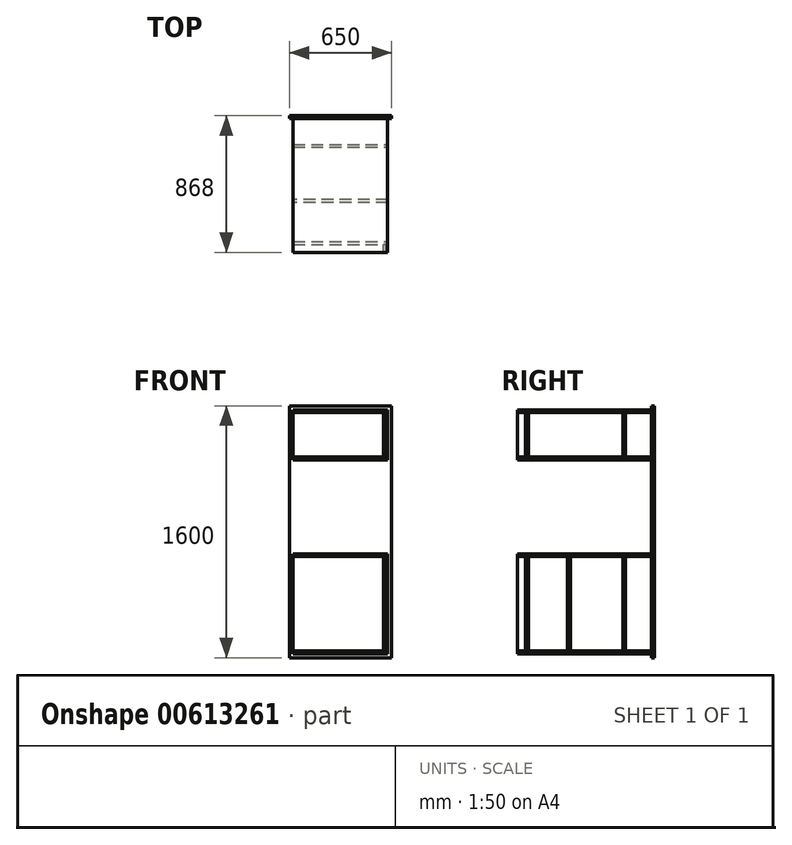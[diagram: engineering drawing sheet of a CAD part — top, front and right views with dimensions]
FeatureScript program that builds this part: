
annotation { "Feature Type Name" : "Feature", "Feature Type Description" : "" }
export const myFeature = defineFeature(function(context is Context, id is Id, definition is map)
    precondition{}
    {
        {
            var Q0;
            Q0=qCreatedBy(makeId("Top.planeOp"),FACE);
            var sketch = newSketch(context, id + "F0", { "sketchPlane" : qUnion([Q0])});
            skLineSegment(sketch, "E0.bottom", {"start": v(-313.84, 645.81) * mm, "end": v(286.16, 645.81) * mm});
            skLineSegment(sketch, "E0.top", {"start": v(-313.84, -204.19) * mm, "end": v(286.16, -204.19) * mm});
            skLineSegment(sketch, "E0.left", {"start": v(-313.84, 645.81) * mm, "end": v(-313.84, -204.19) * mm});
            skLineSegment(sketch, "E0.right", {"start": v(286.16, 645.81) * mm, "end": v(286.16, -204.19) * mm});
            skSolve(sketch);
        }
        {
            var Q0;
            Q0 = qSketchRegion(id + "F0", true);
            extrude(context, id + "F1", {"entities" : qUnion([Q0]), "depth" : 18 * mm, "offsetDistance" : 25 * mm});
        }
        {
            var Q0;
            Q0=makeQuery(id+"F1.opExtrude","SWEPT_FACE",FACE,{"disambiguationData":[OSD([sQuery(id+"F0.wireOp",EDGE,"E0.bottom")])]});
            var sketch = newSketch(context, id + "F2", { "sketchPlane" : qUnion([Q0])});
            skLineSegment(sketch, "E1.bottom", {"start": v(-311.16, 343) * mm, "end": v(338.84, 343) * mm});
            skLineSegment(sketch, "E1.top", {"start": v(-311.16, -1257) * mm, "end": v(338.84, -1257) * mm});
            skLineSegment(sketch, "E1.left", {"start": v(-311.16, 343) * mm, "end": v(-311.16, -1257) * mm});
            skLineSegment(sketch, "E1.right", {"start": v(338.84, 343) * mm, "end": v(338.84, -1257) * mm});
            skSolve(sketch);
        }
        {
            var Q0;
            Q0 = qSketchRegion(id + "F2", true);
            extrude(context, id + "F3", {"entities" : qUnion([Q0]), "depth" : 18 * mm, "offsetDistance" : 25 * mm});
        }
        {
            var Q0;
            Q0=makeQuery(id+"F3.opExtrude","CAP_FACE",FACE,{"disambiguationData":[OSD([sQuery(id+"F2.wireOp",EDGE,"E1.bottom"),sQuery(id+"F2.wireOp",EDGE,"E1.top"),sQuery(id+"F2.wireOp",EDGE,"E1.left"),sQuery(id+"F2.wireOp",EDGE,"E1.right")])],"isStart":true});
            var sketch = newSketch(context, id + "F4", { "sketchPlane" : qUnion([Q0])});
            skLineSegment(sketch, "E2.bottom", {"start": v(-313.84, -596) * mm, "end": v(286.16, -596) * mm});
            skLineSegment(sketch, "E2.top", {"start": v(-313.84, -614) * mm, "end": v(286.16, -614) * mm});
            skLineSegment(sketch, "E2.left", {"start": v(-313.84, -596) * mm, "end": v(-313.84, -614) * mm});
            skLineSegment(sketch, "E2.right", {"start": v(286.16, -596) * mm, "end": v(286.16, -614) * mm});
            skLineSegment(sketch, "E3.bottom", {"start": v(-313.84, -1214) * mm, "end": v(286.16, -1214) * mm});
            skLineSegment(sketch, "E3.top", {"start": v(-313.84, -1232) * mm, "end": v(286.16, -1232) * mm});
            skLineSegment(sketch, "E3.left", {"start": v(-313.84, -1214) * mm, "end": v(-313.84, -1232) * mm});
            skLineSegment(sketch, "E3.right", {"start": v(286.16, -1214) * mm, "end": v(286.16, -1232) * mm});
            skLineSegment(sketch, "E4.bottom", {"start": v(-313.84, 318) * mm, "end": v(286.16, 318) * mm});
            skLineSegment(sketch, "E4.top", {"start": v(-313.84, 300) * mm, "end": v(286.16, 300) * mm});
            skLineSegment(sketch, "E4.left", {"start": v(-313.84, 318) * mm, "end": v(-313.84, 300) * mm});
            skLineSegment(sketch, "E4.right", {"start": v(286.16, 318) * mm, "end": v(286.16, 300) * mm});
            skSolve(sketch);
        }
        {
            var Q0;
            Q0 = qSketchRegion(id + "F4", true);
            var Q1;
            Q1=makeQuery(id+"F1.opExtrude","SWEPT_FACE",FACE,{"disambiguationData":[OSD([sQuery(id+"F0.wireOp",EDGE,"E0.top")])]});
            extrude(context, id + "F5", {"entities" : qUnion([Q0]), "endBound" : BoundingType.UP_TO_SURFACE, "depth" : 25 * mm, "endBoundEntityFace" : qUnion([Q1]), "offsetDistance" : 25 * mm});
        }
        {
            var Q0;
            Q0=makeQuery(id+"F5.opExtrude","SWEPT_FACE",FACE,{"disambiguationData":[OSD([sQuery(id+"F4.wireOp",EDGE,"E3.bottom")])]});
            var sketch = newSketch(context, id + "F6", { "sketchPlane" : qUnion([Q0])});
            skLineSegment(sketch, "E5.bottom", {"start": v(-313.84, -154.19) * mm, "end": v(286.16, -154.19) * mm});
            skLineSegment(sketch, "E5.top", {"start": v(-313.84, -136.19) * mm, "end": v(286.16, -136.19) * mm});
            skLineSegment(sketch, "E5.left", {"start": v(-313.84, -154.19) * mm, "end": v(-313.84, -136.19) * mm});
            skLineSegment(sketch, "E5.right", {"start": v(286.16, -154.19) * mm, "end": v(286.16, -136.19) * mm});
            skLineSegment(sketch, "E6.bottom", {"start": v(-313.84, 463.81) * mm, "end": v(286.16, 463.81) * mm});
            skLineSegment(sketch, "E6.top", {"start": v(-313.84, 481.81) * mm, "end": v(286.16, 481.81) * mm});
            skLineSegment(sketch, "E6.left", {"start": v(-313.84, 463.81) * mm, "end": v(-313.84, 481.81) * mm});
            skLineSegment(sketch, "E6.right", {"start": v(286.16, 463.81) * mm, "end": v(286.16, 481.81) * mm});
            skLineSegment(sketch, "E7.bottom", {"start": v(286.16, 131.81) * mm, "end": v(-313.84, 131.81) * mm});
            skLineSegment(sketch, "E7.top", {"start": v(286.16, 113.81) * mm, "end": v(-313.84, 113.81) * mm});
            skLineSegment(sketch, "E7.left", {"start": v(286.16, 131.81) * mm, "end": v(286.16, 113.81) * mm});
            skLineSegment(sketch, "E7.right", {"start": v(-313.84, 131.81) * mm, "end": v(-313.84, 113.81) * mm});
            skSolve(sketch);
        }
        {
            var Q0;
            Q0 = qSketchRegion(id + "F6", true);
            var Q1;
            Q1=makeQuery(id+"F5.opExtrude","SWEPT_FACE",FACE,{"disambiguationData":[OSD([sQuery(id+"F4.wireOp",EDGE,"E2.top")])]});
            extrude(context, id + "F7", {"entities" : qUnion([Q0]), "endBound" : BoundingType.UP_TO_SURFACE, "depth" : 25 * mm, "endBoundEntityFace" : qUnion([Q1]), "offsetDistance" : 25 * mm});
        }
        {
            var Q0;
            Q0=makeQuery(id+"F1.opExtrude","CAP_FACE",FACE,{"disambiguationData":[OSD([sQuery(id+"F0.wireOp",EDGE,"E0.bottom"),sQuery(id+"F0.wireOp",EDGE,"E0.top"),sQuery(id+"F0.wireOp",EDGE,"E0.left"),sQuery(id+"F0.wireOp",EDGE,"E0.right")])],"isStart":false});
            var sketch = newSketch(context, id + "F8", { "sketchPlane" : qUnion([Q0])});
            skLineSegment(sketch, "E8.bottom", {"start": v(286.16, 481.81) * mm, "end": v(-313.84, 481.81) * mm});
            skLineSegment(sketch, "E8.top", {"start": v(286.16, 463.81) * mm, "end": v(-313.84, 463.81) * mm});
            skLineSegment(sketch, "E8.left", {"start": v(286.16, 481.81) * mm, "end": v(286.16, 463.81) * mm});
            skLineSegment(sketch, "E8.right", {"start": v(-313.84, 481.81) * mm, "end": v(-313.84, 463.81) * mm});
            skLineSegment(sketch, "E9.bottom", {"start": v(286.16, -136.19) * mm, "end": v(-313.84, -136.19) * mm});
            skLineSegment(sketch, "E9.top", {"start": v(286.16, -154.19) * mm, "end": v(-313.84, -154.19) * mm});
            skLineSegment(sketch, "E9.left", {"start": v(286.16, -136.19) * mm, "end": v(286.16, -154.19) * mm});
            skLineSegment(sketch, "E9.right", {"start": v(-313.84, -136.19) * mm, "end": v(-313.84, -154.19) * mm});
            skSolve(sketch);
        }
        {
            var Q0;
            Q0 = qSketchRegion(id + "F8", true);
            var Q1;
            Q1=makeQuery(id+"F5.opExtrude","SWEPT_FACE",FACE,{"disambiguationData":[OSD([sQuery(id+"F4.wireOp",EDGE,"E4.top")])]});
            extrude(context, id + "F9", {"entities" : qUnion([Q0]), "endBound" : BoundingType.UP_TO_SURFACE, "depth" : 25 * mm, "endBoundEntityFace" : qUnion([Q1]), "offsetDistance" : 25 * mm});
        }
        {
            var Q0;
            Q0=makeQuery(id+"F7.opExtrude","SWEPT_FACE",FACE,{"disambiguationData":[OSD([sQuery(id+"F6.wireOp",EDGE,"E5.bottom")])]});
            var sketch = newSketch(context, id + "F10", { "sketchPlane" : qUnion([Q0])});
            skLineSegment(sketch, "E10.bottom", {"start": v(276.16, 300) * mm, "end": v(258.16, 300) * mm});
            skLineSegment(sketch, "E10.top", {"start": v(276.16, 18) * mm, "end": v(258.16, 18) * mm});
            skLineSegment(sketch, "E10.left", {"start": v(276.16, 300) * mm, "end": v(276.16, 18) * mm});
            skLineSegment(sketch, "E10.right", {"start": v(258.16, 300) * mm, "end": v(258.16, 18) * mm});
            skLineSegment(sketch, "E11.bottom", {"start": v(258.16, -614) * mm, "end": v(276.16, -614) * mm});
            skLineSegment(sketch, "E11.top", {"start": v(258.16, -1214) * mm, "end": v(276.16, -1214) * mm});
            skLineSegment(sketch, "E11.left", {"start": v(258.16, -614) * mm, "end": v(258.16, -1214) * mm});
            skLineSegment(sketch, "E11.right", {"start": v(276.16, -614) * mm, "end": v(276.16, -1214) * mm});
            skSolve(sketch);
        }
        {
            var Q0;
            Q0 = qSketchRegion(id + "F10", true);
            var Q1;
            Q1=makeQuery(id+"F5.opExtrude","CAP_FACE",FACE,{"disambiguationData":[OSD([sQuery(id+"F4.wireOp",EDGE,"E4.bottom"),sQuery(id+"F4.wireOp",EDGE,"E4.top"),sQuery(id+"F4.wireOp",EDGE,"E4.left"),sQuery(id+"F4.wireOp",EDGE,"E4.right")])],"isStart":false});
            extrude(context, id + "F11", {"entities" : qUnion([Q0]), "endBound" : BoundingType.UP_TO_SURFACE, "depth" : 25 * mm, "endBoundEntityFace" : qUnion([Q1]), "offsetDistance" : 25 * mm});
        }
    });
